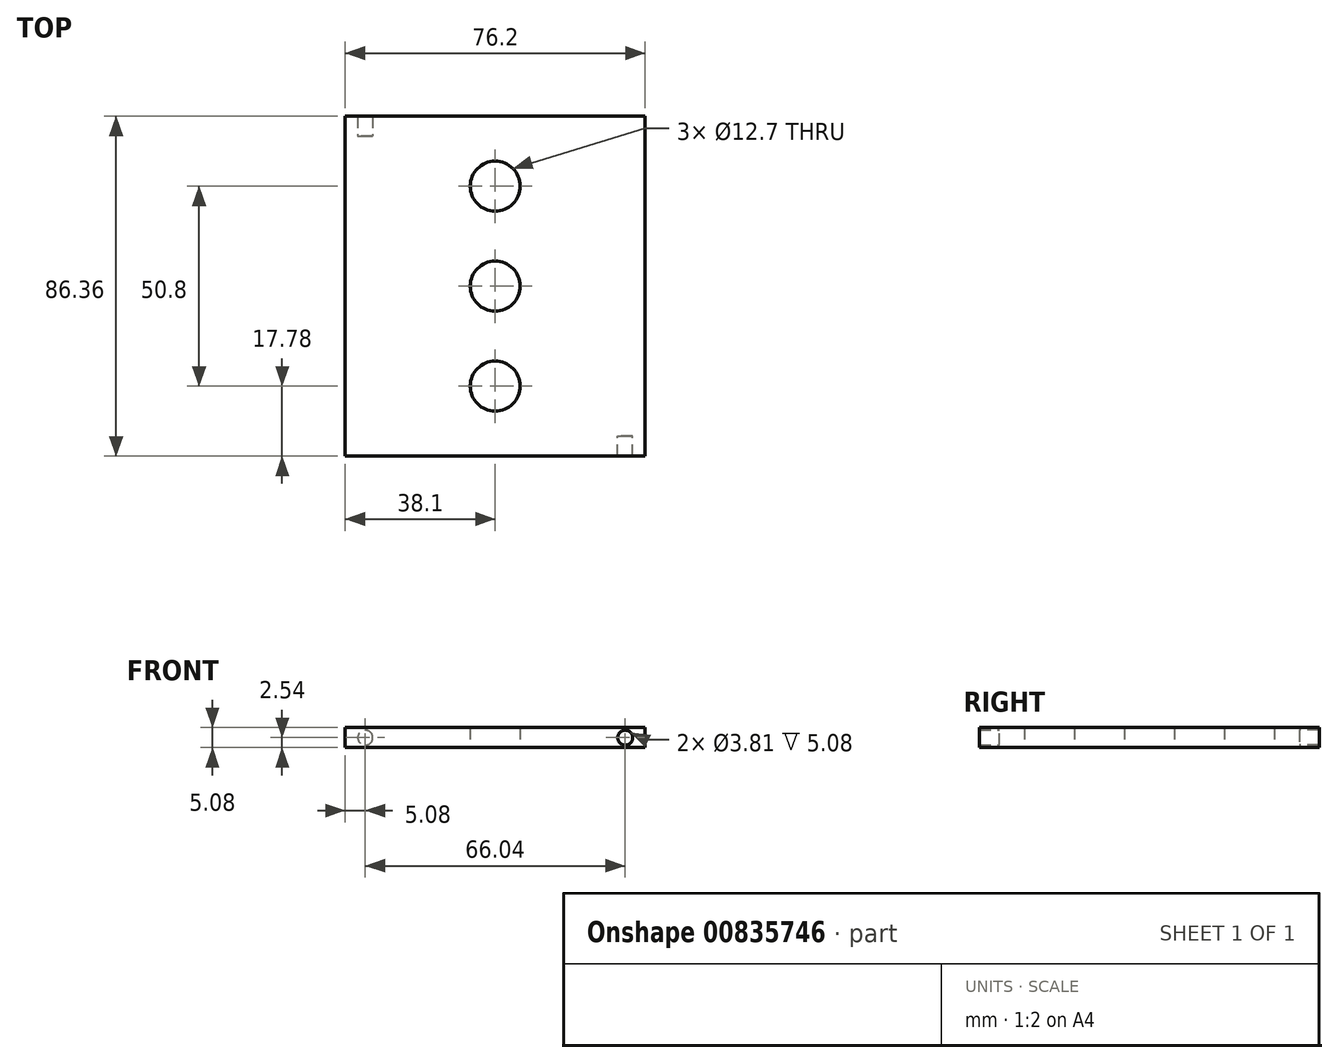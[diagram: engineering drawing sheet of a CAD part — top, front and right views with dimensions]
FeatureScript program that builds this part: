
annotation { "Feature Type Name" : "Feature", "Feature Type Description" : "" }
export const myFeature = defineFeature(function(context is Context, id is Id, definition is map)
    precondition{}
    {
        {
            var Q0;
            Q0=qCreatedBy(makeId("Top.planeOp"),FACE);
            var sketch = newSketch(context, id + "F0", { "sketchPlane" : qUnion([Q0])});
            skLineSegment(sketch, "E0.bottom", {"start": v(-38.1, 38.1) * mm, "end": v(38.1, 38.1) * mm});
            skLineSegment(sketch, "E0.top", {"start": v(-38.1, -38.1) * mm, "end": v(38.1, -38.1) * mm});
            skLineSegment(sketch, "E0.left", {"start": v(-38.1, 38.1) * mm, "end": v(-38.1, -38.1) * mm});
            skLineSegment(sketch, "E0.right", {"start": v(38.1, 38.1) * mm, "end": v(38.1, -38.1) * mm});
            skPoint(sketch, "E0.middle", {"position": v(0, 0) * mm});
            skCircle(sketch, "E1", {"center": v(0, 0) * mm, "radius": 6.35 * mm});
            skCircle(sketch, "E2", {"center": v(0, -25.4) * mm, "radius": 6.35 * mm});
            skCircle(sketch, "E3.MirrorC", {"center": v(0, 25.4) * mm, "radius": 6.35 * mm});
            skSolve(sketch);
        }
        {
            var Q0;
            Q0=makeQuery(id+"F0.imprint","IMPRINT",FACE,{"disambiguationData":[TD([[makeQuery(id+"F0.imprint","IMPRINT",EDGE,{"derivedFrom":sQuery(id+"F0.wireOp",EDGE,"E0.bottom")}),-1.0]])]});
            extrude(context, id + "F1", {"entities" : qUnion([Q0]), "depth" : 5.08 * mm, "offsetDistance" : 25.4 * mm});
        }
        {
            var Q0;
            Q0=makeQuery(id+"F1.opExtrude","SWEPT_FACE",FACE,{"disambiguationData":[OSD([sQuery(id+"F0.wireOp",EDGE,"E0.top")])]});
            var sketch = newSketch(context, id + "F2", { "sketchPlane" : qUnion([Q0])});
            skPoint(sketch, "E4.centerSnap0", {"position": v(-38.1, 2.54) * mm});
            skCircle(sketch, "E5", {"center": v(-33.02, 2.54) * mm, "radius": 1.9 * mm});
            skCircle(sketch, "E6.MirrorC", {"center": v(33.02, 2.54) * mm, "radius": 1.9 * mm});
            skSolve(sketch);
        }
        {
            var Q0;
            Q0=makeQuery(id+"F2.imprint","IMPRINT",FACE,{"disambiguationData":[TD([[makeQuery(id+"F2.imprint","IMPRINT",EDGE,{"derivedFrom":sQuery(id+"F2.wireOp",EDGE,"E5")}),1.0]])]});
            var Q1;
            Q1=makeQuery(id+"F2.imprint","IMPRINT",FACE,{"disambiguationData":[TD([[makeQuery(id+"F2.imprint","IMPRINT",EDGE,{"derivedFrom":sQuery(id+"F2.wireOp",EDGE,"E6.MirrorC")}),-1.0]])]});
            extrude(context, id + "F3", {"entities" : qUnion([Q0, Q1]), "operationType" : NewBodyOperationType.ADD, "depth" : 5.08 * mm, "offsetDistance" : 25.4 * mm});
        }
        {
            var Q0;
            Q0=makeQuery(id+"F1.opExtrude","SWEPT_FACE",FACE,{"disambiguationData":[OSD([sQuery(id+"F0.wireOp",EDGE,"E0.bottom")])]});
            var sketch = newSketch(context, id + "F4", { "sketchPlane" : qUnion([Q0])});
            skCircle(sketch, "E7", {"center": v(-33.02, 2.54) * mm, "radius": 1.9 * mm});
            skCircle(sketch, "E8.MirrorC", {"center": v(33.02, 2.54) * mm, "radius": 1.9 * mm});
            skSolve(sketch);
        }
        {
            var Q0;
            Q0=makeQuery(id+"F4.imprint","IMPRINT",FACE,{"disambiguationData":[TD([[makeQuery(id+"F4.imprint","IMPRINT",EDGE,{"derivedFrom":sQuery(id+"F4.wireOp",EDGE,"E7")}),1.0]])]});
            var Q1;
            Q1=makeQuery(id+"F4.imprint","IMPRINT",FACE,{"disambiguationData":[TD([[makeQuery(id+"F4.imprint","IMPRINT",EDGE,{"derivedFrom":sQuery(id+"F4.wireOp",EDGE,"E8.MirrorC")}),-1.0]])]});
            extrude(context, id + "F5", {"entities" : qUnion([Q0, Q1]), "operationType" : NewBodyOperationType.ADD, "depth" : 5.08 * mm, "offsetDistance" : 25.4 * mm});
        }
    });
